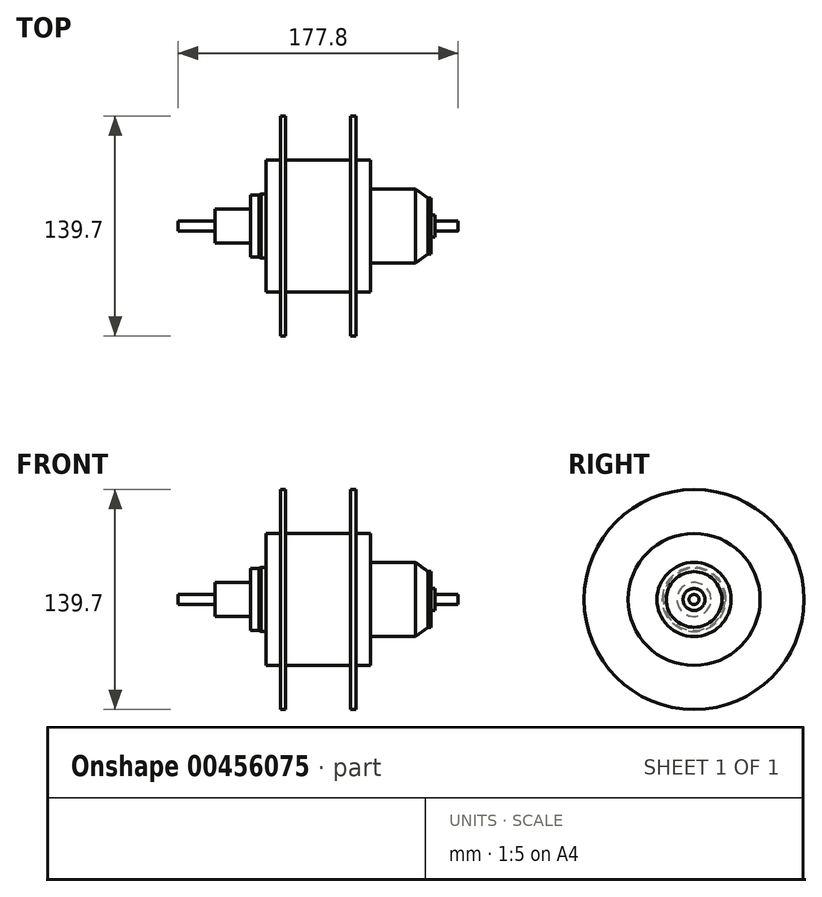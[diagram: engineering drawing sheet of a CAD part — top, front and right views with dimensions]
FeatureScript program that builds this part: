
annotation { "Feature Type Name" : "Feature", "Feature Type Description" : "" }
export const myFeature = defineFeature(function(context is Context, id is Id, definition is map)
    precondition{}
    {
        {
            var Q0;
            Q0=qCreatedBy(makeId("Right.planeOp"),FACE);
            var sketch = newSketch(context, id + "F0", { "sketchPlane" : qUnion([Q0])});
            skCircle(sketch, "E0", {"center": v(0, 0) * mm, "radius": 3.18 * mm});
            skSolve(sketch);
        }
        {
            var Q0;
            Q0=makeQuery(id+"F0.imprint","IMPRINT",FACE,{"disambiguationData":[TD([[makeQuery(id+"F0.imprint","IMPRINT",EDGE,{"derivedFrom":sQuery(id+"F0.wireOp",EDGE,"E0")}),1.0]])]});
            extrude(context, id + "F1", {"entities" : qUnion([Q0]), "depth" : 177.8 * mm, "symmetric" : true});
        }
        {
            var Q0;
            Q0=qCreatedBy(makeId("Front.planeOp"),FACE);
            var sketch = newSketch(context, id + "F2", { "sketchPlane" : qUnion([Q0])});
            skLineSegment(sketch, "E1", {"start": v(0, 0) * mm, "end": v(0, 41.9) * mm, "construction": true});
            skLineSegment(sketch, "E2.0", {"start": v(-88.9, 3.18) * mm, "end": v(-88.9, -3.18) * mm});
            skLineSegment(sketch, "E2.1", {"start": v(88.9, 3.18) * mm, "end": v(88.9, -3.18) * mm});
            skLineSegment(sketch, "E3", {"start": v(-65.57, 3.18) * mm, "end": v(74.13, 3.18) * mm});
            skLineSegment(sketch, "E4", {"start": v(74.13, 3.18) * mm, "end": v(74.13, 6.99) * mm});
            skLineSegment(sketch, "E5", {"start": v(74.13, 6.99) * mm, "end": v(71.55, 6.99) * mm});
            skLineSegment(sketch, "E6", {"start": v(71.55, 6.99) * mm, "end": v(71.55, 17.65) * mm});
            skLineSegment(sketch, "E7", {"start": v(71.55, 17.65) * mm, "end": v(69.83, 17.65) * mm});
            skLineSegment(sketch, "E8", {"start": v(69.83, 17.65) * mm, "end": v(61.84, 23.56) * mm});
            skLineSegment(sketch, "E9", {"start": v(61.84, 23.56) * mm, "end": v(33.2, 23.56) * mm});
            skLineSegment(sketch, "E10", {"start": v(33.2, 23.56) * mm, "end": v(33.2, 41.9) * mm});
            skLineSegment(sketch, "E11", {"start": v(33.2, 41.91) * mm, "end": v(23.92, 41.9) * mm});
            skLineSegment(sketch, "E12", {"start": v(23.92, 41.9) * mm, "end": v(23.92, 69.85) * mm});
            skLineSegment(sketch, "E13", {"start": v(23.92, 69.85) * mm, "end": v(20.62, 69.85) * mm});
            skLineSegment(sketch, "E14", {"start": v(20.62, 69.85) * mm, "end": v(20.62, 41.9) * mm});
            skLineSegment(sketch, "E15", {"start": v(20.62, 41.9) * mm, "end": v(-20.62, 41.9) * mm});
            skLineSegment(sketch, "E16", {"start": v(-20.62, 41.9) * mm, "end": v(-20.62, 69.85) * mm});
            skLineSegment(sketch, "E17", {"start": v(-20.62, 69.85) * mm, "end": v(-23.92, 69.85) * mm});
            skLineSegment(sketch, "E18", {"start": v(-23.92, 69.85) * mm, "end": v(-23.92, 41.9) * mm});
            skLineSegment(sketch, "E19", {"start": v(-23.92, 41.9) * mm, "end": v(-33.2, 41.9) * mm});
            skLineSegment(sketch, "E20", {"start": v(-33.2, 41.9) * mm, "end": v(-33.2, 20.32) * mm});
            skLineSegment(sketch, "E21", {"start": v(-33.2, 20.32) * mm, "end": v(-36.42, 20.32) * mm});
            skLineSegment(sketch, "E22", {"start": v(-36.42, 20.32) * mm, "end": v(-37.5, 19.68) * mm});
            skLineSegment(sketch, "E23", {"start": v(-37.5, 19.69) * mm, "end": v(-43.03, 19.69) * mm});
            skLineSegment(sketch, "E24", {"start": v(-43.03, 19.69) * mm, "end": v(-43.03, 10.79) * mm});
            skLineSegment(sketch, "E25", {"start": v(-43.03, 10.79) * mm, "end": v(-65.57, 10.79) * mm});
            skLineSegment(sketch, "E26", {"start": v(-65.57, 10.79) * mm, "end": v(-65.57, 3.18) * mm});
            skLineSegment(sketch, "E27", {"start": v(0, 0) * mm, "end": v(108.81, 0) * mm, "construction": true});
            skSolve(sketch);
        }
        {
            var Q0;
            Q0=makeQuery(id+"F2.imprint","IMPRINT",FACE,{"disambiguationData":[TD([[makeQuery(id+"F2.imprint","IMPRINT",EDGE,{"derivedFrom":sQuery(id+"F2.wireOp",EDGE,"E3")}),1.0]])]});
            var Q1;
            Q1=sQuery(id+"F2.wireOp",EDGE,"E27");
            revolve(context, id + "F3", {"operationType" : NewBodyOperationType.ADD, "entities" : qUnion([Q0]), "axis" : qUnion([Q1]), "revolveType" : RevolveType.FULL});
        }
    });
